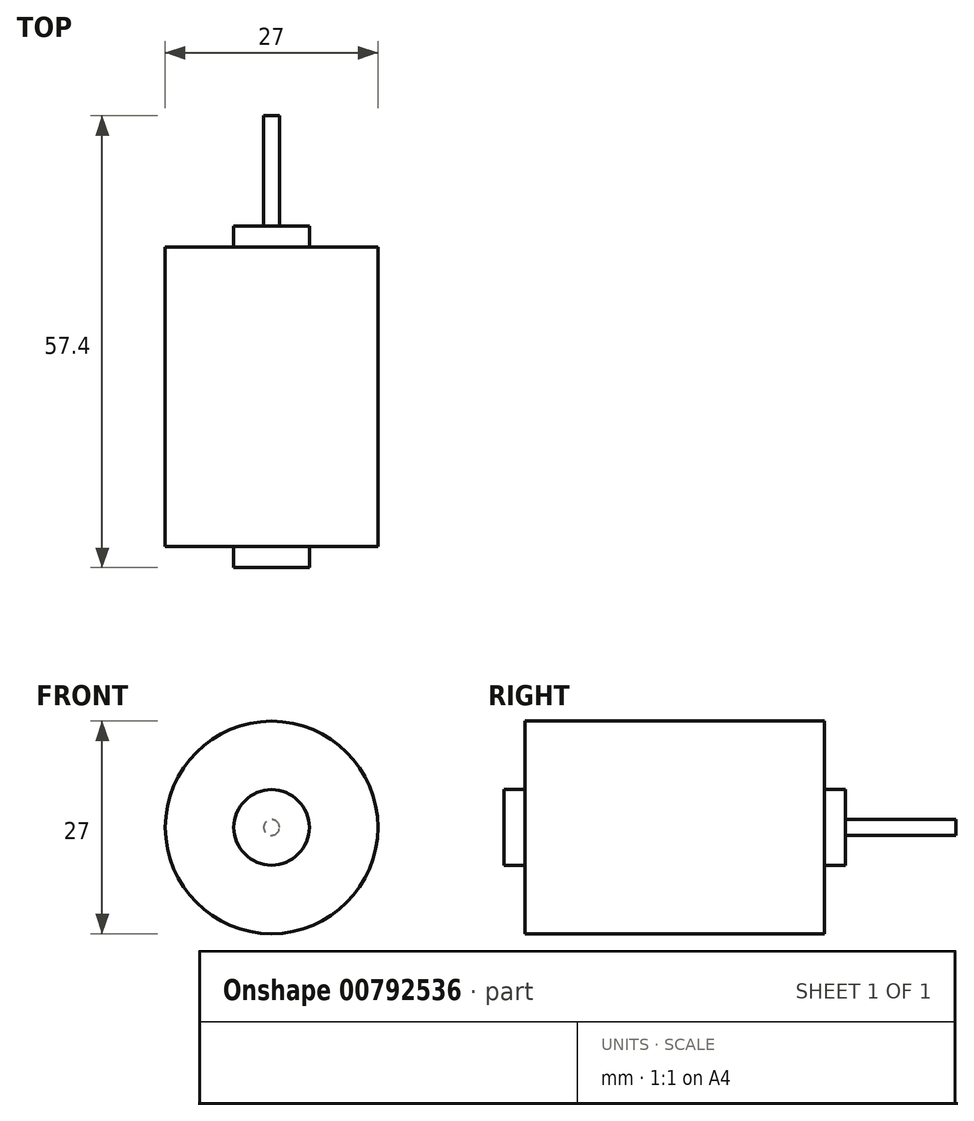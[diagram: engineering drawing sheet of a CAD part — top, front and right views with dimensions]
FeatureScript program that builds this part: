
annotation { "Feature Type Name" : "Feature", "Feature Type Description" : "" }
export const myFeature = defineFeature(function(context is Context, id is Id, definition is map)
    precondition{}
    {
        {
            var Q0;
            Q0=qCreatedBy(makeId("Top.planeOp"),FACE);
            var sketch = newSketch(context, id + "F0", { "sketchPlane" : qUnion([Q0])});
            skLineSegment(sketch, "E0", {"start": v(-13.5, 35.7) * mm, "end": v(-12.5, 35.7) * mm});
            skLineSegment(sketch, "E1", {"start": v(-12.5, 35.7) * mm, "end": v(-12.5, 21.7) * mm});
            skLineSegment(sketch, "E2", {"start": v(-12.5, 21.7) * mm, "end": v(-8.7, 21.7) * mm});
            skLineSegment(sketch, "E3", {"start": v(-8.7, 21.7) * mm, "end": v(-8.7, 19) * mm});
            skLineSegment(sketch, "E4", {"start": v(-8.7, 19) * mm, "end": v(0, 19) * mm});
            skLineSegment(sketch, "E5", {"start": v(0, 19) * mm, "end": v(0, -19) * mm});
            skLineSegment(sketch, "E6", {"start": v(0, -19) * mm, "end": v(-8.7, -19) * mm});
            skLineSegment(sketch, "E7", {"start": v(-8.7, -19) * mm, "end": v(-8.7, -21.7) * mm});
            skLineSegment(sketch, "E8", {"start": v(-8.7, -21.7) * mm, "end": v(-13.5, -21.7) * mm});
            skLineSegment(sketch, "E9", {"start": v(-13.5, -21.7) * mm, "end": v(-13.5, 35.7) * mm});
            skLineSegment(sketch, "E10", {"start": v(-8.7, -19) * mm, "end": v(-13.5, -19) * mm, "construction": true});
            skSolve(sketch);
        }
        {
            var Q0;
            Q0=makeQuery(id+"F0.imprint","IMPRINT",FACE,{"disambiguationData":[TD([[makeQuery(id+"F0.imprint","IMPRINT",EDGE,{"derivedFrom":sQuery(id+"F0.wireOp",EDGE,"E0")}),-1.0]])]});
            var Q1;
            Q1=sQuery(id+"F0.wireOp",EDGE,"E9");
            revolve(context, id + "F1", {"surfaceOperationType" : NewSurfaceOperationType.NEW, "entities" : qUnion([Q0]), "axis" : qUnion([Q1]), "revolveType" : RevolveType.FULL});
        }
    });
